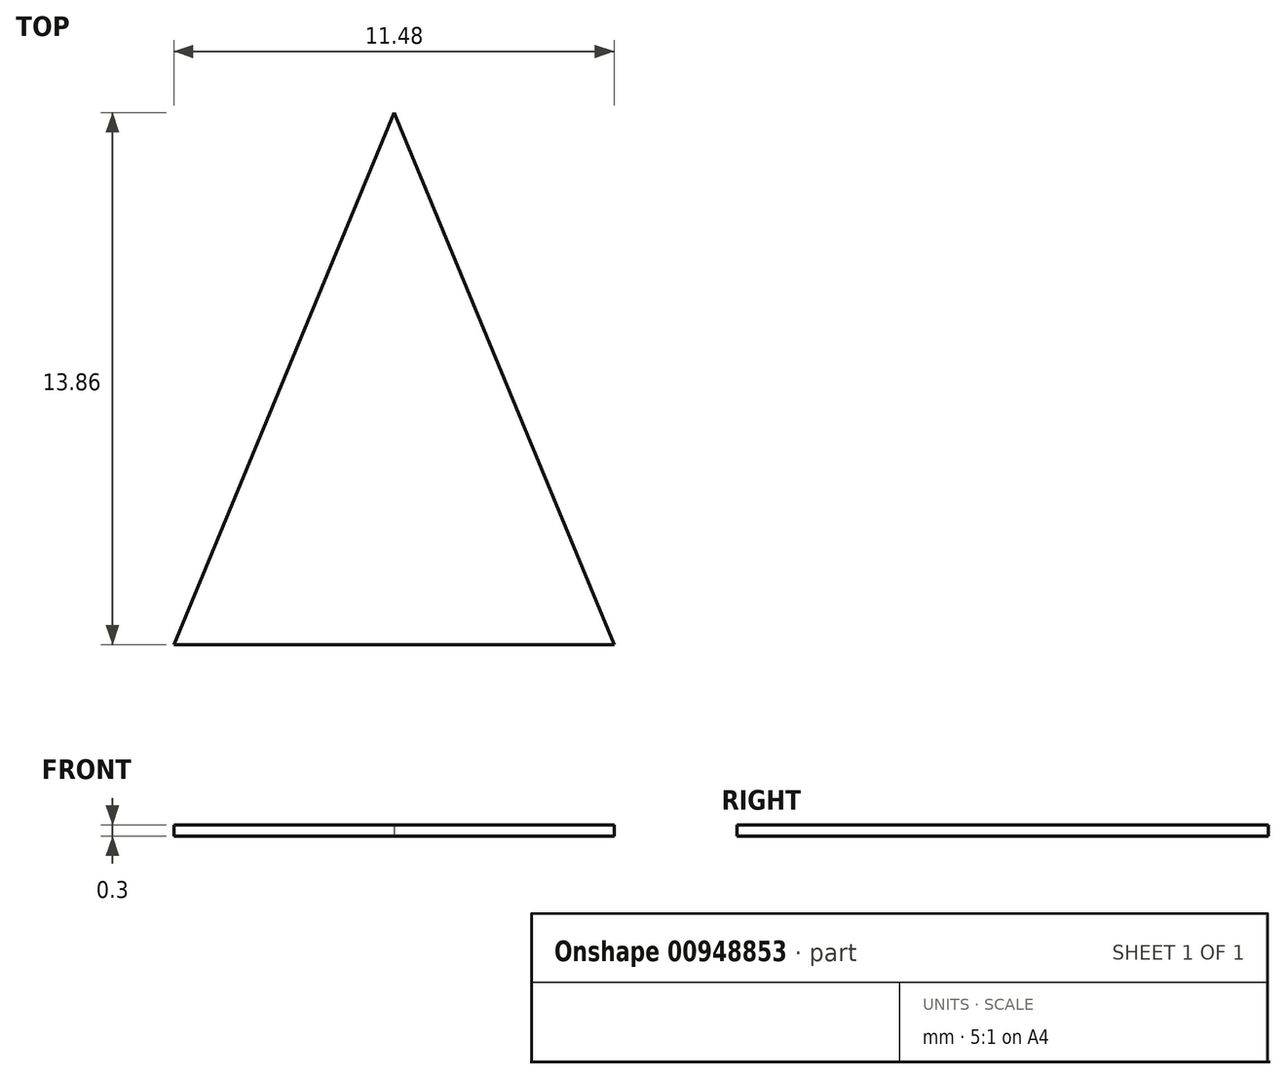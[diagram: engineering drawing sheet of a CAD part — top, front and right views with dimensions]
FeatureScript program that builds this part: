
annotation { "Feature Type Name" : "Feature", "Feature Type Description" : "" }
export const myFeature = defineFeature(function(context is Context, id is Id, definition is map)
    precondition{}
    {
        {
            var Q0;
            Q0=qCreatedBy(makeId("Top.planeOp"),FACE);
            var sketch = newSketch(context, id + "F0", { "sketchPlane" : qUnion([Q0])});
            skLineSegment(sketch, "E0", {"start": v(0, 0) * mm, "end": v(-5.74, -13.86) * mm});
            skLineSegment(sketch, "E1", {"start": v(-5.74, -13.86) * mm, "end": v(5.74, -13.86) * mm});
            skLineSegment(sketch, "E2", {"start": v(5.74, -13.86) * mm, "end": v(0, 0) * mm});
            skSolve(sketch);
        }
        {
            var Q0;
            Q0=makeQuery(id+"F0.imprint","IMPRINT",FACE,{"disambiguationData":[TD([[makeQuery(id+"F0.imprint","IMPRINT",EDGE,{"derivedFrom":sQuery(id+"F0.wireOp",EDGE,"E0")}),1.0]])]});
            extrude(context, id + "F1", {"entities" : qUnion([Q0]), "depth" : 0.3 * mm, "offsetDistance" : 25 * mm});
        }
    });
